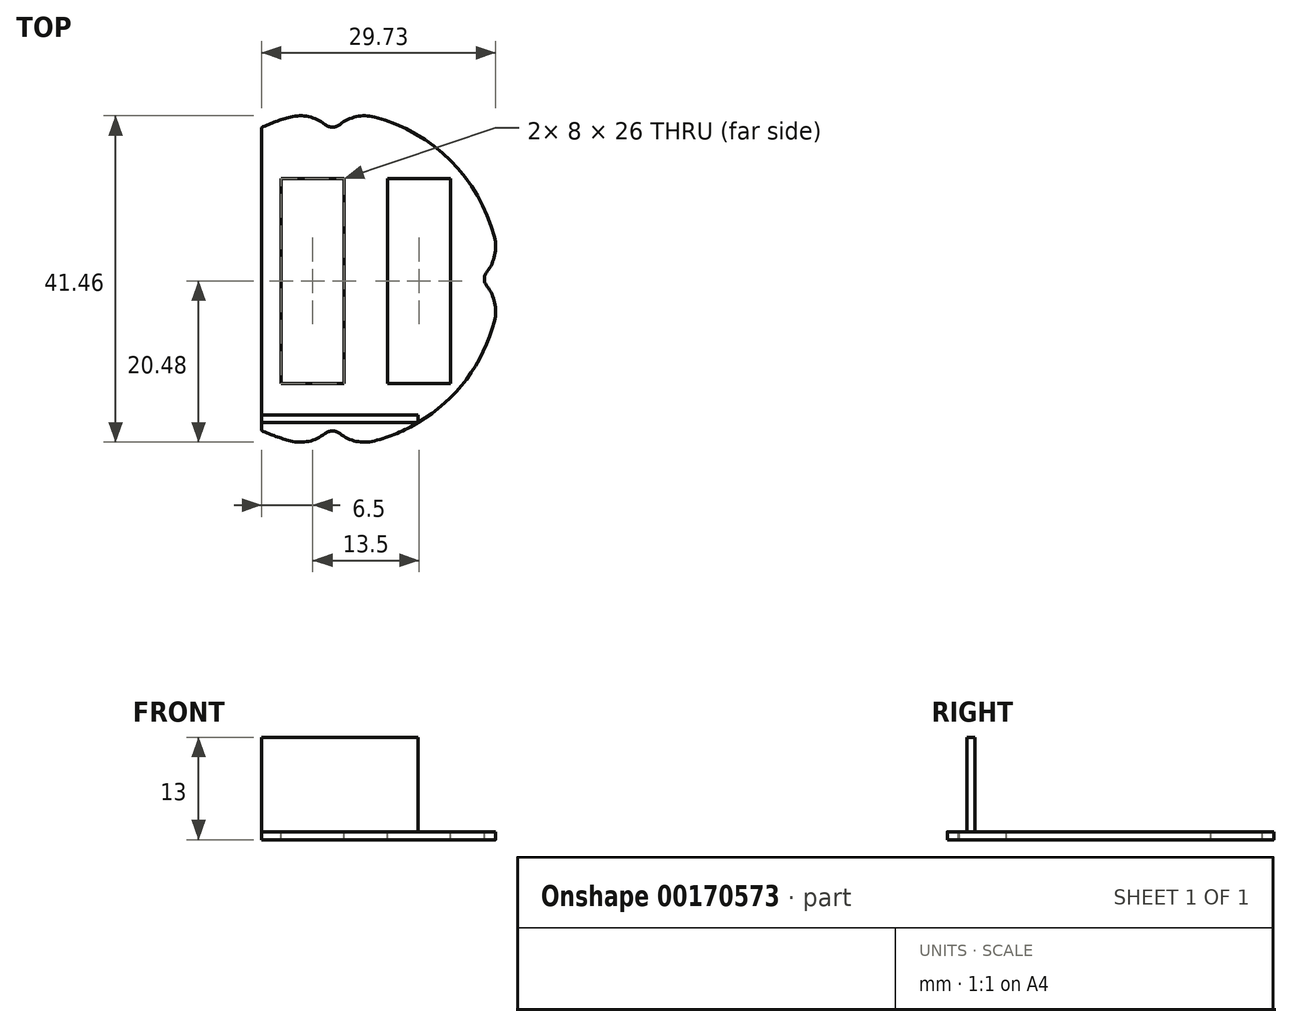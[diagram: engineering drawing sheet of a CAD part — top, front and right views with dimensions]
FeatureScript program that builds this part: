
annotation { "Feature Type Name" : "Feature", "Feature Type Description" : "" }
export const myFeature = defineFeature(function(context is Context, id is Id, definition is map)
    precondition{}
    {
        {
            var Q0;
            Q0=qCreatedBy(makeId("Top.planeOp"),FACE);
            var sketch = newSketch(context, id + "F0", { "sketchPlane" : qUnion([Q0])});
            skArc(sketch, "E0", {"start": v(-9, -19.25) * mm, "mid": v(21.25, 0) * mm, "end": v(-9, 19.25) * mm});
            skLineSegment(sketch, "E1", {"start": v(-9, 19.25) * mm, "end": v(-9, -19.25) * mm});
            skSolve(sketch);
        }
        {
            var Q0;
            Q0=makeQuery(id+"F0.imprint","IMPRINT",FACE,{"disambiguationData":[TD([[makeQuery(id+"F0.imprint","IMPRINT",EDGE,{"derivedFrom":sQuery(id+"F0.wireOp",EDGE,"E0")}),1.0]])]});
            extrude(context, id + "F1", {"entities" : qUnion([Q0]), "depth" : 1 * mm});
        }
        {
            var Q0;
            Q0=makeQuery(id+"F1.opExtrude","CAP_FACE",FACE,{"disambiguationData":[OSD([sQuery(id+"F0.wireOp",EDGE,"E0")])],"isStart":false});
            var sketch = newSketch(context, id + "F2", { "sketchPlane" : qUnion([Q0])});
            skLineSegment(sketch, "E2.left", {"start": v(-10.83, -18.28) * mm, "end": v(-10.83, -18.28) * mm});
            skLineSegment(sketch, "E2.right", {"start": v(10.83, -18.28) * mm, "end": v(10.83, -18.28) * mm});
            skLineSegment(sketch, "E3.bottom", {"start": v(-9, -17.25) * mm, "end": v(10.89, -17.25) * mm});
            skLineSegment(sketch, "E3.top", {"start": v(-9, -18.25) * mm, "end": v(10.89, -18.25) * mm});
            skLineSegment(sketch, "E3.left", {"start": v(-9, -17.25) * mm, "end": v(-9, -18.25) * mm});
            skLineSegment(sketch, "E3.right", {"start": v(10.89, -17.25) * mm, "end": v(10.89, -18.25) * mm});
            skSolve(sketch);
        }
        {
            var Q0;
            Q0 = qSketchRegion(id + "F2", true);
            extrude(context, id + "F3", {"entities" : qUnion([Q0]), "operationType" : NewBodyOperationType.ADD, "depth" : 12 * mm});
        }
        {
            var Q0;
            {var subQ0=sQuery(id+"F0.wireOp",EDGE,"E1");var subQ1=sQuery(id+"F0.wireOp",EDGE,"E0");var subQ2=makeQuery(id+"F1.opExtrude","CAP_FACE",FACE,{"disambiguationData":[OSD([subQ1,subQ0])],"isStart":false});Q0=makeQuery(id+"F3.boolean.opBoolean","SPLIT",FACE,{"disambiguationData":[TD([makeQuery(id+"F1.opExtrude","SWEPT_FACE",FACE,{"disambiguationData":[OSD([subQ1])]}),subQ2,makeQuery(id+"F1.opExtrude","SWEPT_FACE",FACE,{"disambiguationData":[OSD([subQ0])]}),makeQuery(id+"F3.opExtrude","SWEPT_FACE",FACE,{"disambiguationData":[OSD([sQuery(id+"F2.wireOp",EDGE,"E2.top")])]}),makeQuery(id+"F3.opExtrude","SWEPT_FACE",FACE,{"disambiguationData":[OSD([sQuery(id+"F2.wireOp",EDGE,"XM5uAxj4-0acq-6J7y-uhyk-wyFDUd83eVwD")])]}),makeQuery(id+"F3.opExtrude","SWEPT_FACE",FACE,{"disambiguationData":[OSD([sQuery(id+"F2.wireOp",EDGE,"kXPhDjdp-fpOl-levP-tOcx-IgAj81t9NecW")])]}),makeQuery(id+"F3.opExtrude","SWEPT_FACE",FACE,{"disambiguationData":[OSD([sQuery(id+"F2.wireOp",EDGE,"XBPCAe4O-u5II-slJk-ikuj-Vkvm23DPyT5s")])]})])],"derivedFrom":subQ2});}
            var sketch = newSketch(context, id + "F4", { "sketchPlane" : qUnion([Q0])});
            skLineSegment(sketch, "E4.bottom", {"start": v(-6.5, 12.75) * mm, "end": v(1.5, 12.75) * mm});
            skLineSegment(sketch, "E4.top", {"start": v(-6.5, -13.25) * mm, "end": v(1.5, -13.25) * mm});
            skLineSegment(sketch, "E4.left", {"start": v(-6.5, 12.75) * mm, "end": v(-6.5, -13.25) * mm});
            skLineSegment(sketch, "E4.right", {"start": v(1.5, 12.75) * mm, "end": v(1.5, -13.25) * mm});
            skLineSegment(sketch, "E5.bottom", {"start": v(7, 12.75) * mm, "end": v(15, 12.75) * mm});
            skLineSegment(sketch, "E5.top", {"start": v(7, -13.25) * mm, "end": v(15, -13.25) * mm});
            skLineSegment(sketch, "E5.left", {"start": v(7, 12.75) * mm, "end": v(7, -13.25) * mm});
            skLineSegment(sketch, "E5.right", {"start": v(15, 12.75) * mm, "end": v(15, -13.25) * mm});
            skSolve(sketch);
        }
        {
            var Q0;
            Q0 = qSketchRegion(id + "F4", true);
            extrude(context, id + "F5", {"entities" : qUnion([Q0]), "operationType" : NewBodyOperationType.REMOVE, "endBound" : BoundingType.THROUGH_ALL, "oppositeDirection" : true, "depth" : 25 * mm});
        }
        {
            var Q0;
            {var subQ0=sQuery(id+"F0.wireOp",EDGE,"E1");var subQ1=sQuery(id+"F0.wireOp",EDGE,"E0");var subQ2=makeQuery(id+"F1.opExtrude","CAP_FACE",FACE,{"disambiguationData":[OSD([subQ1,subQ0])],"isStart":false});Q0=makeQuery(id+"F3.boolean.opBoolean","SPLIT",FACE,{"disambiguationData":[TD([makeQuery(id+"F1.opExtrude","SWEPT_FACE",FACE,{"disambiguationData":[OSD([subQ1])]}),subQ2,makeQuery(id+"F1.opExtrude","SWEPT_FACE",FACE,{"disambiguationData":[OSD([subQ0])]}),makeQuery(id+"F3.opExtrude","SWEPT_FACE",FACE,{"disambiguationData":[OSD([sQuery(id+"F2.wireOp",EDGE,"E3.bottom")])]}),makeQuery(id+"F3.opExtrude","SWEPT_FACE",FACE,{"disambiguationData":[OSD([sQuery(id+"F2.wireOp",EDGE,"E3.top")])]}),makeQuery(id+"F3.opExtrude","SWEPT_FACE",FACE,{"disambiguationData":[OSD([sQuery(id+"F2.wireOp",EDGE,"E3.left")])]}),makeQuery(id+"F3.opExtrude","SWEPT_FACE",FACE,{"disambiguationData":[OSD([sQuery(id+"F2.wireOp",EDGE,"E3.right")])]})])],"derivedFrom":subQ2});}
            var sketch = newSketch(context, id + "F6", { "sketchPlane" : qUnion([Q0])});
            skCircle(sketch, "E6", {"center": v(0, -20.8) * mm, "radius": 1.5 * mm});
            skCircle(sketch, "E7.1.0", {"center": v(20.8, 0) * mm, "radius": 1.5 * mm});
            skCircle(sketch, "E7.2.0", {"center": v(0, 20.8) * mm, "radius": 1.5 * mm});
            skCircle(sketch, "E7.3.0", {"center": v(-20.8, 0) * mm, "radius": 1.5 * mm});
            skPoint(sketch, "E7.center", {"position": v(0, 0) * mm});
            skSolve(sketch);
        }
        {
            var Q0;
            Q0 = qSketchRegion(id + "F6", true);
            extrude(context, id + "F7", {"entities" : qUnion([Q0]), "operationType" : NewBodyOperationType.REMOVE, "endBound" : BoundingType.THROUGH_ALL, "oppositeDirection" : true, "depth" : 25 * mm});
        }
        {
            var Q0;
            Q0=makeQuery(id+"F7.boolean.opBoolean","INTERSECT",EDGE,{"disambiguationData":[OD(0.0)],"derivedFrom":[makeQuery(id+"F1.opExtrude","SWEPT_FACE",FACE,{"disambiguationData":[OSD([sQuery(id+"F0.wireOp",EDGE,"E0")])]}),makeQuery(id+"F7.opExtrude","SWEPT_FACE",FACE,{"disambiguationData":[OSD([sQuery(id+"F6.wireOp",EDGE,"E6")])]})]});
            var Q1;
            Q1=makeQuery(id+"F7.boolean.opBoolean","INTERSECT",EDGE,{"disambiguationData":[OD(1.0)],"derivedFrom":[makeQuery(id+"F1.opExtrude","SWEPT_FACE",FACE,{"disambiguationData":[OSD([sQuery(id+"F0.wireOp",EDGE,"E0")])]}),makeQuery(id+"F7.opExtrude","SWEPT_FACE",FACE,{"disambiguationData":[OSD([sQuery(id+"F6.wireOp",EDGE,"E6")])]})]});
            var Q2;
            Q2=makeQuery(id+"F7.boolean.opBoolean","INTERSECT",EDGE,{"disambiguationData":[OD(0.0)],"derivedFrom":[makeQuery(id+"F1.opExtrude","SWEPT_FACE",FACE,{"disambiguationData":[OSD([sQuery(id+"F0.wireOp",EDGE,"E0")])]}),makeQuery(id+"F7.opExtrude","SWEPT_FACE",FACE,{"disambiguationData":[OSD([sQuery(id+"F6.wireOp",EDGE,"E7.1.0")])]})]});
            var Q3;
            Q3=makeQuery(id+"F7.boolean.opBoolean","INTERSECT",EDGE,{"disambiguationData":[OD(1.0)],"derivedFrom":[makeQuery(id+"F1.opExtrude","SWEPT_FACE",FACE,{"disambiguationData":[OSD([sQuery(id+"F0.wireOp",EDGE,"E0")])]}),makeQuery(id+"F7.opExtrude","SWEPT_FACE",FACE,{"disambiguationData":[OSD([sQuery(id+"F6.wireOp",EDGE,"E7.1.0")])]})]});
            var Q4;
            Q4=makeQuery(id+"F7.boolean.opBoolean","INTERSECT",EDGE,{"disambiguationData":[OD(0.0)],"derivedFrom":[makeQuery(id+"F1.opExtrude","SWEPT_FACE",FACE,{"disambiguationData":[OSD([sQuery(id+"F0.wireOp",EDGE,"E0")])]}),makeQuery(id+"F7.opExtrude","SWEPT_FACE",FACE,{"disambiguationData":[OSD([sQuery(id+"F6.wireOp",EDGE,"E7.2.0")])]})]});
            var Q5;
            Q5=makeQuery(id+"F7.boolean.opBoolean","INTERSECT",EDGE,{"disambiguationData":[OD(1.0)],"derivedFrom":[makeQuery(id+"F1.opExtrude","SWEPT_FACE",FACE,{"disambiguationData":[OSD([sQuery(id+"F0.wireOp",EDGE,"E0")])]}),makeQuery(id+"F7.opExtrude","SWEPT_FACE",FACE,{"disambiguationData":[OSD([sQuery(id+"F6.wireOp",EDGE,"E7.2.0")])]})]});
            fillet(context, id + "F8", {"entities" : qUnion([Q0, Q1, Q2, Q3, Q4, Q5]), "radius" : 5 * mm, "tangentPropagation" : true, "allowEdgeOverflow" : false});
        }
    });
